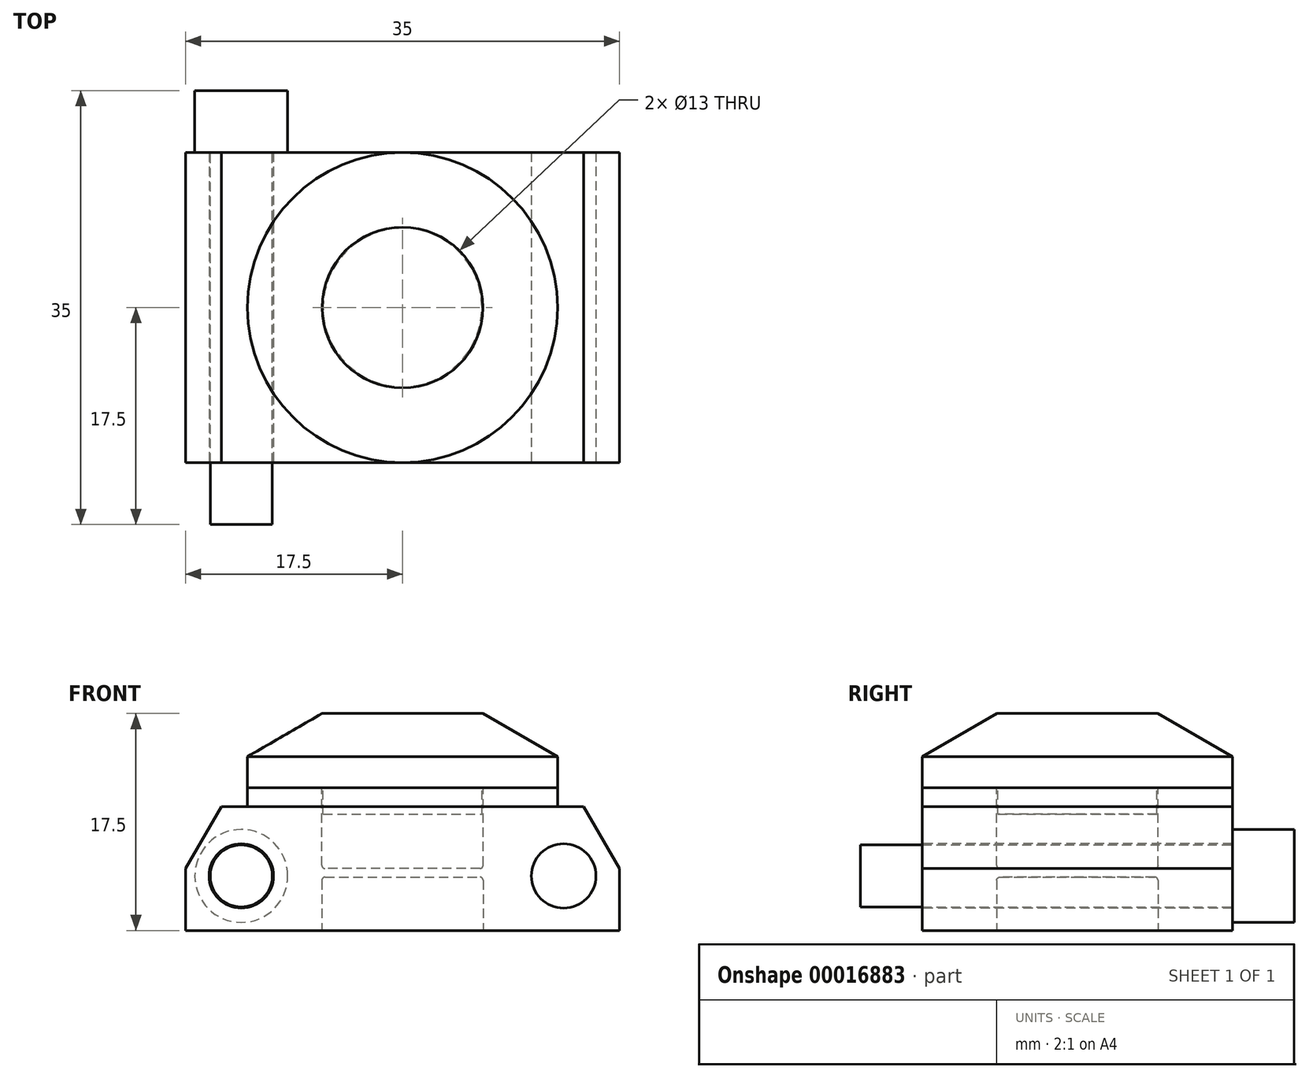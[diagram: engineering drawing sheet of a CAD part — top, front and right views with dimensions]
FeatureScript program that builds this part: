
annotation { "Feature Type Name" : "Feature", "Feature Type Description" : "" }
export const myFeature = defineFeature(function(context is Context, id is Id, definition is map)
    precondition{}
    {
        {
            var Q0;
            Q0=qCreatedBy(makeId("Top.planeOp"),FACE);
            var sketch = newSketch(context, id + "F0", { "sketchPlane" : qUnion([Q0])});
            skLineSegment(sketch, "E0.rect.bottom", {"start": v(-17.5, 12.5) * mm, "end": v(17.5, 12.5) * mm});
            skLineSegment(sketch, "E0.rect.top", {"start": v(-17.5, -12.5) * mm, "end": v(17.5, -12.5) * mm});
            skLineSegment(sketch, "E0.rect.left", {"start": v(-17.5, 12.5) * mm, "end": v(-17.5, -12.5) * mm});
            skLineSegment(sketch, "E0.rect.right", {"start": v(17.5, 12.5) * mm, "end": v(17.5, -12.5) * mm});
            skPoint(sketch, "E0.rect.middle", {"position": v(0, 0) * mm});
            skSolve(sketch);
        }
        {
            var Q0;
            Q0=makeQuery(id+"F0.imprint","IMPRINT",FACE,{"disambiguationData":[TD([[makeQuery(id+"F0.imprint","IMPRINT",EDGE,{"derivedFrom":sQuery(id+"F0.wireOp",EDGE,"E0.rect.bottom")}),-1.0]])]});
            extrude(context, id + "F1", {"entities" : qUnion([Q0]), "depth" : 10 * mm});
        }
        {
            var Q0;
            Q0=makeQuery(id+"F1.opExtrude","CAP_FACE",FACE,{"disambiguationData":[OSD([sQuery(id+"F0.wireOp",EDGE,"E0.rect.bottom"),sQuery(id+"F0.wireOp",EDGE,"E0.rect.top"),sQuery(id+"F0.wireOp",EDGE,"E0.rect.left"),sQuery(id+"F0.wireOp",EDGE,"E0.rect.right")])],"isStart":false});
            var sketch = newSketch(context, id + "F2", { "sketchPlane" : qUnion([Q0])});
            skCircle(sketch, "E1", {"center": v(0, 0) * mm, "radius": 12.5 * mm});
            skSolve(sketch);
        }
        {
            var Q0;
            Q0 = qSketchRegion(id + "F2", true);
            extrude(context, id + "F3", {"entities" : qUnion([Q0]), "operationType" : NewBodyOperationType.ADD, "depth" : 1.5 * mm});
        }
        {
            var Q0;
            Q0=makeQuery(id+"F3.opExtrude","CAP_FACE",FACE,{"disambiguationData":[OSD([sQuery(id+"F2.wireOp",EDGE,"E1")])],"isStart":false});
            var sketch = newSketch(context, id + "F4", { "sketchPlane" : qUnion([Q0])});
            skCircle(sketch, "E2", {"center": v(0, 0) * mm, "radius": 6.5 * mm});
            skSolve(sketch);
        }
        {
            var Q0;
            Q0 = qSketchRegion(id + "F4", true);
            extrude(context, id + "F5", {"entities" : qUnion([Q0]), "operationType" : NewBodyOperationType.REMOVE, "oppositeDirection" : true, "depth" : 6.5 * mm});
        }
        {
            var Q0;
            Q0=makeQuery(id+"F5.boolean.opBoolean","COPY",FACE,{"derivedFrom":makeQuery(id+"F5.opExtrude","CAP_FACE",FACE,{"disambiguationData":[OSD([sQuery(id+"F4.wireOp",EDGE,"E2")])],"isStart":false})});
            fillet(context, id + "F6", {"entities" : qUnion([Q0]), "radius" : 0.25 * mm, "tangentPropagation" : true, "allowEdgeOverflow" : false});
        }
        {
            var Q0;
            Q0=makeQuery(id+"F1.opExtrude","CAP_FACE",FACE,{"disambiguationData":[OSD([sQuery(id+"F0.wireOp",EDGE,"E0.rect.bottom"),sQuery(id+"F0.wireOp",EDGE,"E0.rect.top"),sQuery(id+"F0.wireOp",EDGE,"E0.rect.left"),sQuery(id+"F0.wireOp",EDGE,"E0.rect.right")])],"isStart":true});
            var sketch = newSketch(context, id + "F7", { "sketchPlane" : qUnion([Q0])});
            skCircle(sketch, "E3", {"center": v(0, 0) * mm, "radius": 6.5 * mm});
            skSolve(sketch);
        }
        {
            var Q0;
            Q0 = qSketchRegion(id + "F7", true);
            extrude(context, id + "F8", {"entities" : qUnion([Q0]), "operationType" : NewBodyOperationType.REMOVE, "oppositeDirection" : true, "depth" : 4.3 * mm});
        }
        {
            var Q0;
            Q0=makeQuery(id+"F8.boolean.opBoolean","COPY",FACE,{"derivedFrom":makeQuery(id+"F8.opExtrude","CAP_FACE",FACE,{"disambiguationData":[OSD([sQuery(id+"F7.wireOp",EDGE,"E3")])],"isStart":false})});
            fillet(context, id + "F9", {"entities" : qUnion([Q0]), "radius" : 0.25 * mm, "tangentPropagation" : true, "allowEdgeOverflow" : false});
        }
        {
            var Q0;
            Q0=makeQuery(id+"F1.opExtrude","SWEPT_FACE",FACE,{"disambiguationData":[OSD([sQuery(id+"F0.wireOp",EDGE,"E0.rect.top")])]});
            var sketch = newSketch(context, id + "F10", { "sketchPlane" : qUnion([Q0])});
            skLineSegment(sketch, "E4", {"start": v(13, 11.4) * mm, "end": v(13, -2.25) * mm, "construction": true});
            skLineSegment(sketch, "E5", {"start": v(-13, 11.6) * mm, "end": v(-13, -2.05) * mm, "construction": true});
            skLineSegment(sketch, "E6", {"start": v(-21.92, 4.4) * mm, "end": v(24.12, 4.4) * mm, "construction": true});
            skCircle(sketch, "E7", {"center": v(-13, 4.4) * mm, "radius": 2.6 * mm});
            skCircle(sketch, "E8", {"center": v(13, 4.4) * mm, "radius": 2.6 * mm});
            skLineSegment(sketch, "E9", {"start": v(17.5, 5) * mm, "end": v(14.61, 10) * mm});
            skLineSegment(sketch, "E10", {"start": v(14.61, 10) * mm, "end": v(19, 10) * mm});
            skLineSegment(sketch, "E11", {"start": v(19, 10) * mm, "end": v(17.5, 5) * mm});
            skLineSegment(sketch, "E12", {"start": v(0, 0) * mm, "end": v(0, 13.14) * mm, "construction": true});
            skLineSegment(sketch, "E13.MirrorCS", {"start": v(-17.5, 5) * mm, "end": v(-14.61, 10) * mm});
            skLineSegment(sketch, "E14.MirrorCS", {"start": v(-14.61, 10) * mm, "end": v(-19, 10) * mm});
            skLineSegment(sketch, "E15.MirrorCS", {"start": v(-19, 10) * mm, "end": v(-17.5, 5) * mm});
            skSolve(sketch);
        }
        {
            var Q0;
            Q0 = qSketchRegion(id + "F10", true);
            extrude(context, id + "F11", {"entities" : qUnion([Q0]), "operationType" : NewBodyOperationType.REMOVE, "endBound" : BoundingType.THROUGH_ALL, "oppositeDirection" : true, "depth" : 25 * mm});
        }
        {
            var Q0;
            Q0=makeQuery(id+"F3.opExtrude","CAP_FACE",FACE,{"disambiguationData":[OSD([sQuery(id+"F2.wireOp",EDGE,"E1")])],"isStart":false});
            var sketch = newSketch(context, id + "F12", { "sketchPlane" : qUnion([Q0])});
            skCircle(sketch, "E16", {"center": v(0, 0) * mm, "radius": 12.5 * mm});
            skSolve(sketch);
        }
        {
            var Q0;
            Q0 = qSketchRegion(id + "F12", true);
            extrude(context, id + "F13", {"entities" : qUnion([Q0]), "depth" : 6 * mm});
        }
        {
            var Q0;
            Q0=qCreatedBy(makeId("Front.planeOp"),FACE);
            var sketch = newSketch(context, id + "F14", { "sketchPlane" : qUnion([Q0])});
            skLineSegment(sketch, "E17", {"start": v(0, 0) * mm, "end": v(0, 18.78) * mm, "construction": true});
            skLineSegment(sketch, "E18.0", {"start": v(-12.5, 17.5) * mm, "end": v(12.5, 17.5) * mm});
            skLineSegment(sketch, "E19", {"start": v(6.49, 17.5) * mm, "end": v(12.94, 13.77) * mm});
            skLineSegment(sketch, "E20", {"start": v(12.94, 13.77) * mm, "end": v(12.94, 17.5) * mm});
            skLineSegment(sketch, "E21", {"start": v(12.94, 17.5) * mm, "end": v(6.49, 17.5) * mm});
            skSolve(sketch);
        }
        {
            var Q0;
            Q0 = qSketchRegion(id + "F14", true);
            var Q1;
            Q1=sQuery(id+"F14.wireOp",EDGE,"E17");
            revolve(context, id + "F15", {"operationType" : NewBodyOperationType.REMOVE, "entities" : qUnion([Q0]), "axis" : qUnion([Q1]), "revolveType" : RevolveType.FULL});
        }
        {
            var Q0;
            Q0=makeQuery(id+"F13.opExtrude","CAP_FACE",FACE,{"disambiguationData":[OSD([sQuery(id+"F12.wireOp",EDGE,"E16")])],"isStart":true});
            var sketch = newSketch(context, id + "F16", { "sketchPlane" : qUnion([Q0])});
            skCircle(sketch, "E22", {"center": v(0, 0) * mm, "radius": 6.4 * mm});
            skSolve(sketch);
        }
        {
            var Q0;
            Q0 = qSketchRegion(id + "F16", true);
            extrude(context, id + "F17", {"entities" : qUnion([Q0]), "operationType" : NewBodyOperationType.ADD, "depth" : 2.1 * mm});
        }
        {
            var Q0;
            Q0=makeQuery(id+"F1.opExtrude","SWEPT_FACE",FACE,{"disambiguationData":[OSD([sQuery(id+"F0.wireOp",EDGE,"E0.rect.bottom")])]});
            var sketch = newSketch(context, id + "F18", { "sketchPlane" : qUnion([Q0])});
            skCircle(sketch, "E23", {"center": v(13, 4.4) * mm, "radius": 3.75 * mm});
            skSolve(sketch);
        }
        {
            var Q0;
            Q0 = qSketchRegion(id + "F18", true);
            extrude(context, id + "F19", {"entities" : qUnion([Q0]), "depth" : 5 * mm});
        }
        {
            var Q0;
            Q0=makeQuery(id+"F1.opExtrude","SWEPT_FACE",FACE,{"disambiguationData":[OSD([sQuery(id+"F0.wireOp",EDGE,"E0.rect.bottom")])]});
            var sketch = newSketch(context, id + "F20", { "sketchPlane" : qUnion([Q0])});
            skCircle(sketch, "E24", {"center": v(13, 4.4) * mm, "radius": 2.5 * mm});
            skSolve(sketch);
        }
        {
            var Q0;
            Q0 = qSketchRegion(id + "F20", true);
            extrude(context, id + "F21", {"entities" : qUnion([Q0]), "operationType" : NewBodyOperationType.ADD, "oppositeDirection" : true, "depth" : 30 * mm});
        }
    });
